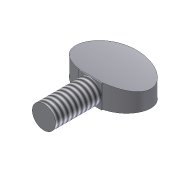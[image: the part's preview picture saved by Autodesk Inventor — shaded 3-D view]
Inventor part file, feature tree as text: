
AUTODESK INVENTOR PART (.ipt)
format: ipt  version: unknown  size: 211,456 bytes
history: native  units: mm (DEFAULTED — no unit token found)
features: extrude x4, sketch x4, projected_geometry x2, plane x1, thread x1
ambient origin geometry x8: Origin, YZ Plane, XZ Plane, XY Plane, X Axis, Y Axis, Z Axis, Center Point
feature tree (12):
  extrude  "Extrusion1"  Depth=12.7mm TaperAngle=0.0deg
  extrude  "Extrusion2"  Depth=3.175mm
  extrude  "Extrusion3"  Depth=10.3124mm
  plane  "Work Plane1"
  extrude  "Extrusion4"  Depth=12.7mm TaperAngle=0.0deg
  thread  "Thread1"  [1 undecoded]
  sketch  "Sketch1"  dims[d0=6.35mm d1=12.7mm d2=0.0mm]
  sketch  "Sketch2"  dims[d3=3.175mm d4=3.175mm]
  sketch  "Sketch3"  dims[d5=20.6248mm d6=10.3124mm]
  projected_geometry  "Projected Loop1"
  sketch  "Sketch4"  dims[d7=12.7mm d8=0.0mm d9=12.7mm d10=0.0mm d11=-12.7mm d12=22.381543mm d13=22.381543mm d14=25.4mm d15=0.0mm d16=25.4mm d17=0.0mm]
  projected_geometry  "Projected Loop2"
note: 1 required parameter value undecoded (feature->parameter linkage not recoverable at this tier; creation-order binding heuristic only, values carry confidence <= 0.55)
